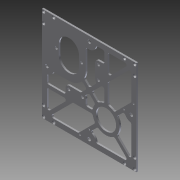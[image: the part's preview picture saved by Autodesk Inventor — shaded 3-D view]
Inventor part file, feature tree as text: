
AUTODESK INVENTOR PART (.ipt)
format: ipt  version: 2012 (Build 160160000, 160)  size: 427,520 bytes
history: native  units: in
note: dims shown in document units (in); Inventor stores cm internally (conversion verified against a paired STEP export)
features: hole x4, fillet x3, sketch x1, extrude x1, chamfer x1
ambient origin geometry x8: Origin, YZ Plane, XZ Plane, XY Plane, X Axis, Y Axis, Z Axis, Center Point
feature tree (10):
  sketch  "Sketch1"  dims[d0=4.5in d1=7.0in d2=7.0in d3=4.5in d4=1.5in d5=2.25in d6=2.25in d10=0.125in d12=0.125in d15=0.125in d16=0.875in d19=0.125in d20=0.875in d23=0.125in d24=0.125in d25=0.875in d26=0.125in d27=0.125in d28=0.125in d29=0.125in d30=0.875in d34=0.125in d35=0.125in d36=0.125in d37=0.125in d38=0.875in d39=0.125in d40=0.125in d47=0.125in d48=0.125in d49=0.125in d50=0.125in d51=0.875in d52=0.125in d87=1.5in d88=1.625in d89=1.5in d91=2.0in d95=0.75in d98=0.9375in d99=0.9375in d112=1.0in d113=2.813in d114=2.0in d122=2.813in d123=1.0in d124=1.5in d140=1.0in d141=1.0in d142=1.0in d143=1.0in d160=0.25in d163=0.25in d167=0.375in d168=0.375in d169=1.25in d171=6.25in d172=6.25in d173=0.375in d174=0.375in d177=3.625in d180=45.0deg d182=0.25in d183=0.25in d186=0.25in d188=0.25in d190=0.125in d195=0.125in d197=0.125in d198=0.25in d204=0.125in d205=0.125in d206=0.25in d207=0.125in d208=0.25in d209=0.125in d211=90.0deg d212=0.25in d217=0.125in d218=3.5in d219=1.0in d220=0.5in d221=1.375in d222=0.5in d223=1.375in d224=0.125in d225=0.0in d226=0.125in d227=0.2in d228=0.75in d229=0.375in d230=0.25in d231=0.5635in d232=1.0in d233=0.8108in d234=1.75in d235=1.0in d236=0.125in d237=0.75in d238=0.375in d239=0.25in d240=0.5635in d241=1.0in d242=0.8108in d243=1.875in d244=1.0in d245=0.125in d246=0.75in d247=0.375in d248=0.25in d249=0.5635in d250=1.0in d251=0.8108in d252=0.0625in d253=0.125in d254=45.0deg d255=0.5in d257=3.5in d258=0.5in d259=3.5in d260=0.5in d261=3.25in d262=3.5in d263=0.5in d264=0.25in d265=0.75in d266=0.375in d267=0.25in d268=0.5635in d269=1.0in d270=0.8108in d271=0.125in d273=0.125in]
  extrude  "Extrusion8"  Depth=7.0in
  fillet  "Fillet3"  Radius=7.0in
  hole  "Hole5"  [1 undecoded]
  hole  "Hole6"  [1 undecoded]
  hole  "Hole7"  [1 undecoded]
  chamfer  "Chamfer1"  Distance=2.25in
  hole  "Hole8"  [1 undecoded]
  fillet  "Fillet4"  Radius=0.125in
  fillet  "Fillet5"  Radius=0.125in
note: 4 required parameter values undecoded (feature->parameter linkage not recoverable at this tier; creation-order binding heuristic only, values carry confidence <= 0.55)
